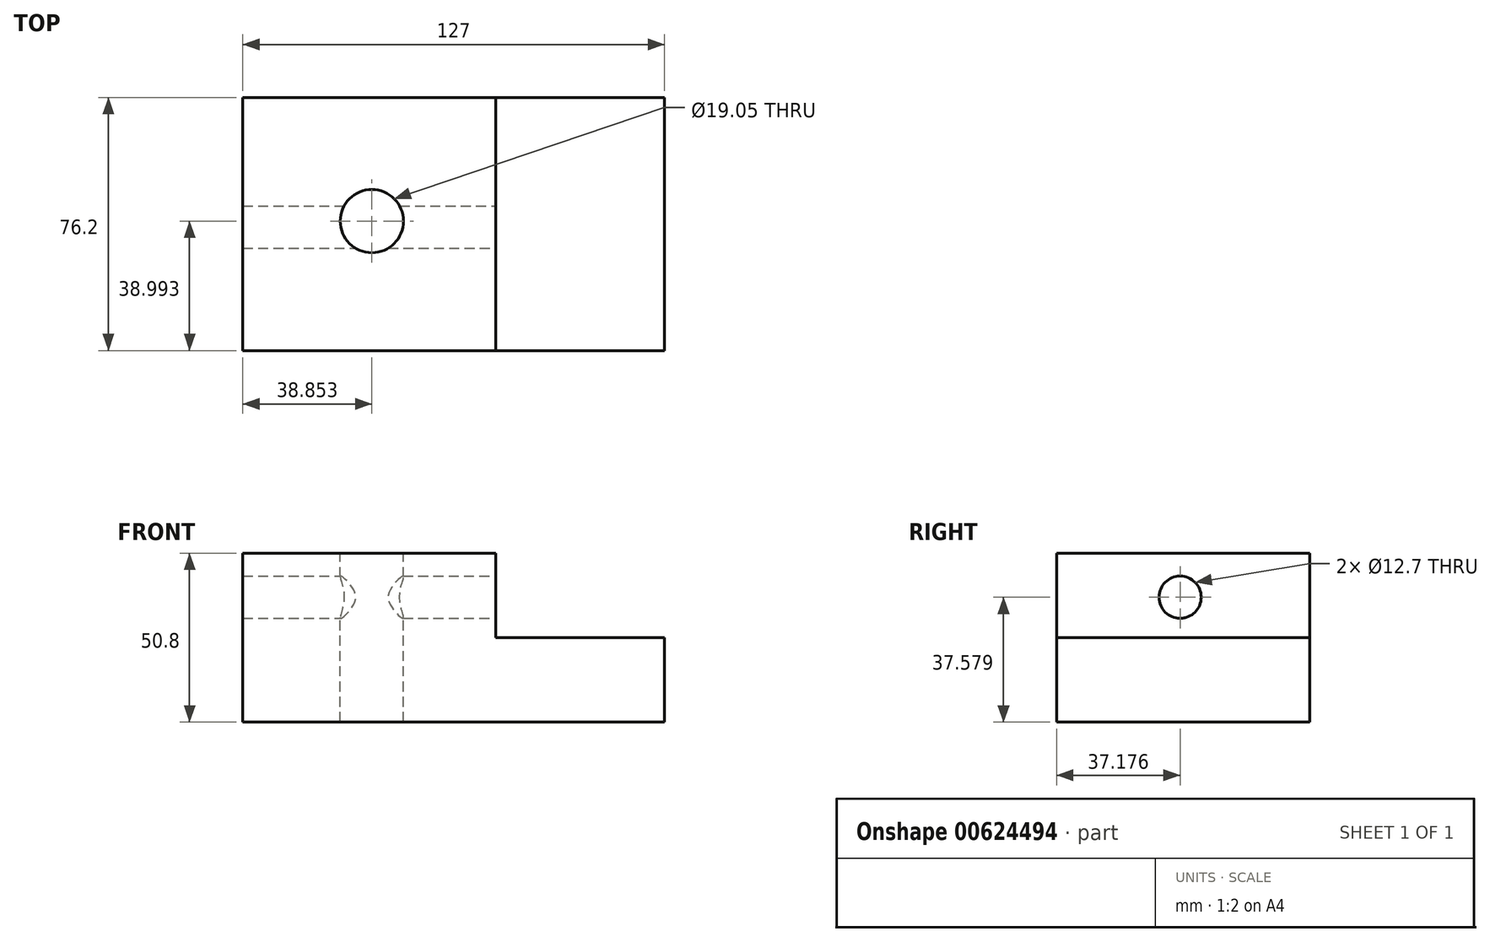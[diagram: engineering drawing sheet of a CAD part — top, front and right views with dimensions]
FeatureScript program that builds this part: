
annotation { "Feature Type Name" : "Feature", "Feature Type Description" : "" }
export const myFeature = defineFeature(function(context is Context, id is Id, definition is map)
    precondition{}
    {
        {
            var Q0;
            Q0=qCreatedBy(makeId("Front.planeOp"),FACE);
            var sketch = newSketch(context, id + "F0", { "sketchPlane" : qUnion([Q0])});
            skLineSegment(sketch, "E0.bottom", {"start": v(0, 0) * mm, "end": v(127, 0) * mm});
            skLineSegment(sketch, "E0.top", {"start": v(0, 50.8) * mm, "end": v(76.2, 50.8) * mm});
            skLineSegment(sketch, "E0.left", {"start": v(0, 0) * mm, "end": v(0, 50.8) * mm});
            skLineSegment(sketch, "E0.right", {"start": v(127, 0) * mm, "end": v(127, 25.4) * mm});
            skLineSegment(sketch, "E1.top", {"start": v(127, 25.4) * mm, "end": v(76.2, 25.4) * mm});
            skLineSegment(sketch, "E1.right", {"start": v(76.2, 50.8) * mm, "end": v(76.2, 25.4) * mm});
            skSolve(sketch);
        }
        {
            var Q0;
            Q0 = qSketchRegion(id + "F0", true);
            extrude(context, id + "F1", {"entities" : qUnion([Q0]), "depth" : 76.2 * mm, "offsetDistance" : 25.4 * mm});
        }
        {
            var Q0;
            Q0 = qSketchRegion(id + "F0", true);
            extrude(context, id + "F2", {"entities" : qUnion([Q0]), "operationType" : NewBodyOperationType.ADD, "depth" : 25.4 * mm, "offsetDistance" : 25.4 * mm});
        }
        {
            var Q0;
            Q0=makeQuery(id+"F1.opExtrude","SWEPT_FACE",FACE,{"disambiguationData":[OSD([sQuery(id+"F0.wireOp",EDGE,"E0.top")])]});
            var sketch = newSketch(context, id + "F3", { "sketchPlane" : qUnion([Q0])});
            skCircle(sketch, "E2", {"center": v(38.85, -37.2) * mm, "radius": 9.3 * mm});
            skSolve(sketch);
        }
        {
            var Q0;
            Q0=sQuery(id+"F3.wireOp",VERTEX,"E2.center");
            var Q1;
            Q1=makeQuery(id+"F1.opExtrude","SWEPT_BODY",BODY,{"disambiguationData":[OSD([sQuery(id+"F0.wireOp",EDGE,"E0.bottom"),sQuery(id+"F0.wireOp",EDGE,"E0.top"),sQuery(id+"F0.wireOp",EDGE,"E0.left"),sQuery(id+"F0.wireOp",EDGE,"E0.right"),sQuery(id+"F0.wireOp",EDGE,"E1.top"),sQuery(id+"F0.wireOp",EDGE,"E1.right")])]});
            hole(context, id + "F4", {"style" : HoleStyle.SIMPLE, "endStyle" : HoleEndStyle.THROUGH, "holeDiameter" : 19.05 * mm, "majorDiameter" : 6.35 * mm, "isTappedThrough" : true, "tappedDepth" : 12.7 * mm, "tapClearance" : 3, "locations" : qUnion([Q0]), "scope" : qUnion([Q1])});
        }
        {
            var Q0;
            Q0=makeQuery(id+"F1.opExtrude","SWEPT_FACE",FACE,{"disambiguationData":[OSD([sQuery(id+"F0.wireOp",EDGE,"E1.right")])]});
            var sketch = newSketch(context, id + "F5", { "sketchPlane" : qUnion([Q0])});
            skCircle(sketch, "E3", {"center": v(-39.02, 37.58) * mm, "radius": 6.23 * mm});
            skSolve(sketch);
        }
        {
            var Q0;
            Q0=sQuery(id+"F5.wireOp",VERTEX,"E3.center");
            var Q1;
            Q1=makeQuery(id+"F1.opExtrude","SWEPT_BODY",BODY,{"disambiguationData":[OSD([sQuery(id+"F0.wireOp",EDGE,"E0.bottom"),sQuery(id+"F0.wireOp",EDGE,"E0.top"),sQuery(id+"F0.wireOp",EDGE,"E0.left"),sQuery(id+"F0.wireOp",EDGE,"E0.right"),sQuery(id+"F0.wireOp",EDGE,"E1.top"),sQuery(id+"F0.wireOp",EDGE,"E1.right")])]});
            hole(context, id + "F6", {"style" : HoleStyle.SIMPLE, "endStyle" : HoleEndStyle.THROUGH, "holeDiameter" : 12.7 * mm, "majorDiameter" : 6.35 * mm, "isTappedThrough" : true, "tappedDepth" : 12.7 * mm, "tapClearance" : 3, "locations" : qUnion([Q0]), "scope" : qUnion([Q1])});
        }
    });
